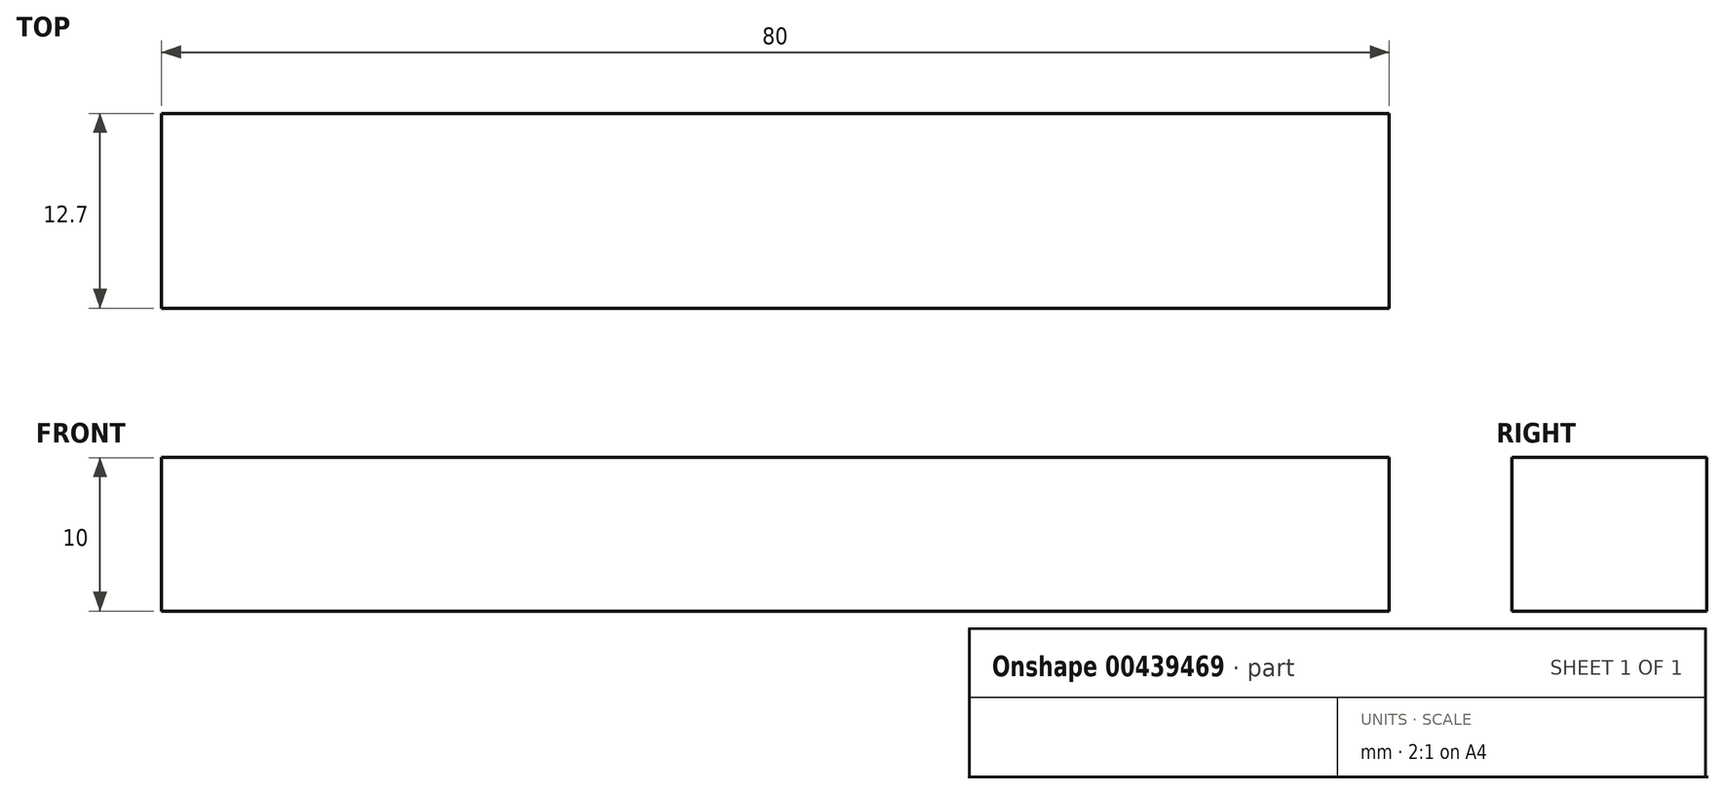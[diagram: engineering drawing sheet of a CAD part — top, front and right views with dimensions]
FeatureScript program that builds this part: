
annotation { "Feature Type Name" : "Feature", "Feature Type Description" : "" }
export const myFeature = defineFeature(function(context is Context, id is Id, definition is map)
    precondition{}
    {
        {
            var Q0;
            Q0=qCreatedBy(makeId("Front.planeOp"),FACE);
            var sketch = newSketch(context, id + "F0", { "sketchPlane" : qUnion([Q0])});
            skLineSegment(sketch, "E0.bottom", {"start": v(40, 5) * mm, "end": v(-40, 5) * mm});
            skLineSegment(sketch, "E0.top", {"start": v(40, -5) * mm, "end": v(-40, -5) * mm});
            skLineSegment(sketch, "E0.left", {"start": v(40, 5) * mm, "end": v(40, -5) * mm});
            skLineSegment(sketch, "E0.right", {"start": v(-40, 5) * mm, "end": v(-40, -5) * mm});
            skPoint(sketch, "E0.middle", {"position": v(0, 0) * mm});
            skSolve(sketch);
        }
        {
            var Q0;
            Q0 = qSketchRegion(id + "F0", true);
            extrude(context, id + "F1", {"entities" : qUnion([Q0]), "depth" : 12.7 * mm});
        }
    });
